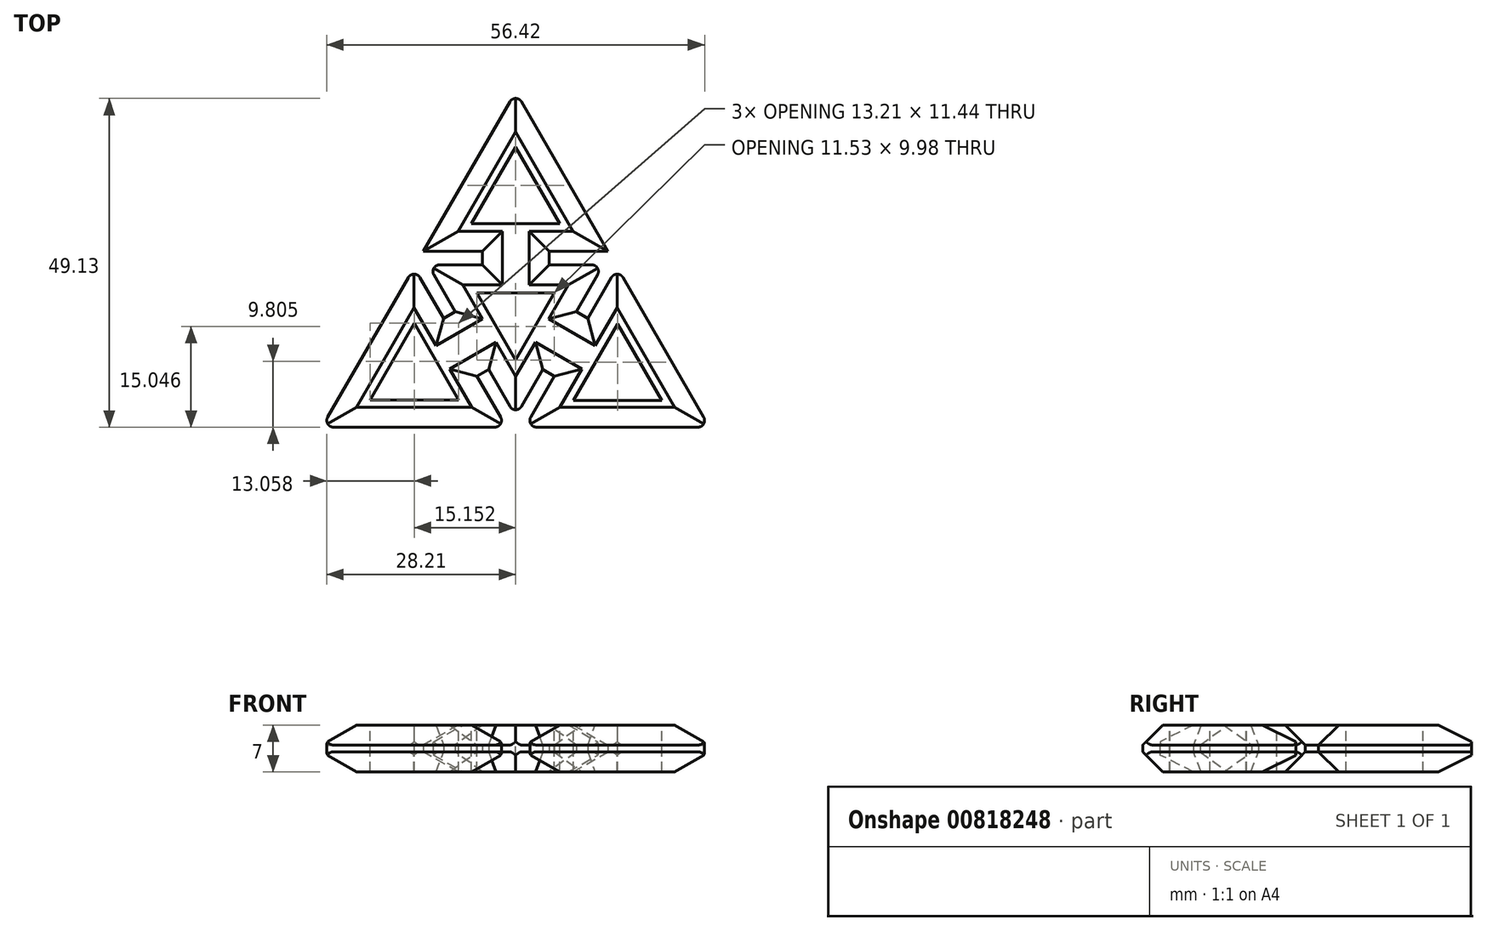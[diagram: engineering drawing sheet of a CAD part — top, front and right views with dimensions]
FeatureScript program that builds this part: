
annotation { "Feature Type Name" : "Feature", "Feature Type Description" : "" }
export const myFeature = defineFeature(function(context is Context, id is Id, definition is map)
    precondition{}
    {
        {
            var Q0;
            Q0=qCreatedBy(makeId("Top.planeOp"),FACE);
            var sketch = newSketch(context, id + "F0", { "sketchPlane" : qUnion([Q0])});
            skLineSegment(sketch, "E0.0", {"start": v(33.1, -19.1) * mm, "end": v(-33.1, -19.1) * mm});
            skLineSegment(sketch, "E0.1", {"start": v(-33.1, -19.1) * mm, "end": v(0, 38.22) * mm});
            skLineSegment(sketch, "E0.2", {"start": v(0, 38.22) * mm, "end": v(33.1, -19.1) * mm});
            skPoint(sketch, "E0.0.midPoint", {"position": v(0, -19.1) * mm});
            skLineSegment(sketch, "E1", {"start": v(0, 38.22) * mm, "end": v(0, -19.1) * mm});
            skLineSegment(sketch, "E2", {"start": v(0, -19.1) * mm, "end": v(-16.55, 9.55) * mm});
            skLineSegment(sketch, "E3", {"start": v(0, -19.1) * mm, "end": v(16.55, 9.55) * mm});
            skLineSegment(sketch, "E4", {"start": v(-16.55, 9.55) * mm, "end": v(16.55, 9.55) * mm});
            skPoint(sketch, "E0.cCircle.center.orphan", {"position": v(0, 0) * mm});
            skLineSegment(sketch, "E5.0", {"start": v(-13.08, 7.55) * mm, "end": v(13.08, 7.55) * mm});
            skLineSegment(sketch, "E5.1", {"start": v(0, -15.1) * mm, "end": v(-13.08, 7.55) * mm});
            skLineSegment(sketch, "E5.2", {"start": v(0, -15.1) * mm, "end": v(13.08, 7.55) * mm});
            skLineSegment(sketch, "E6", {"start": v(-8.27, -4.78) * mm, "end": v(-6.54, -3.78) * mm});
            skLineSegment(sketch, "E7", {"start": v(8.27, -4.78) * mm, "end": v(6.54, -3.78) * mm});
            skLineSegment(sketch, "E8", {"start": v(0, 9.55) * mm, "end": v(0, 7.55) * mm});
            skLineSegment(sketch, "E9.0", {"start": v(-6.38, -9.46) * mm, "end": v(-4.04, -8.1) * mm});
            skLineSegment(sketch, "E10.0", {"start": v(-11.38, -0.8) * mm, "end": v(-9.04, 0.55) * mm});
            skLineSegment(sketch, "E11.0", {"start": v(11.38, -0.8) * mm, "end": v(9.04, 0.55) * mm});
            skLineSegment(sketch, "E12.0", {"start": v(6.38, -9.46) * mm, "end": v(4.04, -8.1) * mm});
            skLineSegment(sketch, "E13.0", {"start": v(-5, 10.25) * mm, "end": v(-5, 7.55) * mm});
            skLineSegment(sketch, "E14.0", {"start": v(5, 10.25) * mm, "end": v(5, 7.55) * mm});
            skLineSegment(sketch, "E15.0", {"start": v(-28.94, -16.7) * mm, "end": v(0, 33.42) * mm});
            skLineSegment(sketch, "E15.1", {"start": v(28.94, -16.7) * mm, "end": v(-28.94, -16.7) * mm});
            skLineSegment(sketch, "E15.2", {"start": v(0, 33.42) * mm, "end": v(28.94, -16.7) * mm});
            skSolve(sketch);
        }
        {
            var Q0;
            {var subQ0=sQuery(id+"F0.wireOp",EDGE,"E5.1");var subQ2=sQuery(id+"F0.wireOp",EDGE,"E5.0");var subQ3=makeQuery(id+"F0.imprint","INTERSECT",VERTEX,{"derivedFrom":[subQ2,subQ0]});Q0=makeQuery(id+"F0.imprint","IMPRINT",FACE,{"disambiguationData":[TD([[makeQuery(id+"F0.imprint","IMPRINT",EDGE,{"disambiguationData":[TD([[subQ3,-1.0]])],"derivedFrom":subQ2}),-1.0]])]});}
            var Q1;
            {var subQ4=sQuery(id+"F0.wireOp",EDGE,"E5.0");var subQ5=makeQuery(id+"F0.imprint","INTERSECT",VERTEX,{"derivedFrom":[subQ4,sQuery(id+"F0.wireOp",EDGE,"E14.0")]});Q1=makeQuery(id+"F0.imprint","IMPRINT",FACE,{"disambiguationData":[TD([[makeQuery(id+"F0.imprint","IMPRINT",EDGE,{"disambiguationData":[TD([[subQ5,-1.0]])],"derivedFrom":subQ4}),-1.0]])]});}
            var Q2;
            {var subQ3=sQuery(id+"F0.wireOp",EDGE,"E6");Q2=makeQuery(id+"F0.imprint","IMPRINT",FACE,{"disambiguationData":[TD([[makeQuery(id+"F0.imprint","IMPRINT",EDGE,{"derivedFrom":subQ3}),1.0]])]});}
            var Q3;
            {var subQ0=sQuery(id+"F0.wireOp",EDGE,"E6");Q3=makeQuery(id+"F0.imprint","IMPRINT",FACE,{"disambiguationData":[TD([[makeQuery(id+"F0.imprint","IMPRINT",EDGE,{"derivedFrom":subQ0}),-1.0]])]});}
            var Q4;
            {var subQ0=sQuery(id+"F0.wireOp",EDGE,"E7");Q4=makeQuery(id+"F0.imprint","IMPRINT",FACE,{"disambiguationData":[TD([[makeQuery(id+"F0.imprint","IMPRINT",EDGE,{"derivedFrom":subQ0}),-1.0]])]});}
            var Q5;
            {var subQ0=sQuery(id+"F0.wireOp",EDGE,"E7");Q5=makeQuery(id+"F0.imprint","IMPRINT",FACE,{"disambiguationData":[TD([[makeQuery(id+"F0.imprint","IMPRINT",EDGE,{"derivedFrom":subQ0}),1.0]])]});}
            var Q6;
            {var subQ0=sQuery(id+"F0.wireOp",EDGE,"E4");var subQ1=sQuery(id+"F0.wireOp",EDGE,"E1");var subQ2=makeQuery(id+"F0.imprint","INTERSECT",VERTEX,{"derivedFrom":[subQ1,subQ0]});Q6=makeQuery(id+"F0.imprint","IMPRINT",FACE,{"disambiguationData":[TD([[makeQuery(id+"F0.imprint","IMPRINT",EDGE,{"disambiguationData":[TD([[subQ2,-1.0]])],"derivedFrom":subQ1}),1.0]])]});}
            var Q7;
            {var subQ0=sQuery(id+"F0.wireOp",EDGE,"E4");var subQ1=sQuery(id+"F0.wireOp",EDGE,"E1");var subQ2=makeQuery(id+"F0.imprint","INTERSECT",VERTEX,{"derivedFrom":[subQ1,subQ0]});Q7=makeQuery(id+"F0.imprint","IMPRINT",FACE,{"disambiguationData":[TD([[makeQuery(id+"F0.imprint","IMPRINT",EDGE,{"disambiguationData":[TD([[subQ2,-1.0]])],"derivedFrom":subQ1}),-1.0]])]});}
            var Q8;
            {var subQ0=sQuery(id+"F0.wireOp",EDGE,"E2");var subQ3=makeQuery(id+"F0.imprint","INTERSECT",VERTEX,{"derivedFrom":[subQ0,sQuery(id+"F0.wireOp",EDGE,"E10.0")]});Q8=makeQuery(id+"F0.imprint","IMPRINT",FACE,{"disambiguationData":[TD([[makeQuery(id+"F0.imprint","IMPRINT",EDGE,{"disambiguationData":[TD([[subQ3,-1.0]])],"derivedFrom":subQ0}),1.0]])]});}
            var Q9;
            {var subQ0=sQuery(id+"F0.wireOp",EDGE,"E3");var subQ4=sQuery(id+"F0.wireOp",EDGE,"E15.1");var subQ5=makeQuery(id+"F0.imprint","INTERSECT",VERTEX,{"derivedFrom":[subQ0,subQ4]});Q9=makeQuery(id+"F0.imprint","IMPRINT",FACE,{"disambiguationData":[TD([[makeQuery(id+"F0.imprint","IMPRINT",EDGE,{"disambiguationData":[TD([[subQ5,-1.0]])],"derivedFrom":subQ0}),-1.0]])]});}
            var Q10;
            {var subQ3=sQuery(id+"F0.wireOp",EDGE,"E4");var subQ5=makeQuery(id+"F0.imprint","INTERSECT",VERTEX,{"derivedFrom":[subQ3,sQuery(id+"F0.wireOp",EDGE,"E14.0")]});Q10=makeQuery(id+"F0.imprint","IMPRINT",FACE,{"disambiguationData":[TD([[makeQuery(id+"F0.imprint","IMPRINT",EDGE,{"disambiguationData":[TD([[subQ5,-1.0]])],"derivedFrom":subQ3}),1.0]])]});}
            var Q11;
            {var subQ0=sQuery(id+"F0.wireOp",EDGE,"E15.0");var subQ3=sQuery(id+"F0.wireOp",EDGE,"E4");var subQ6=makeQuery(id+"F0.imprint","INTERSECT",VERTEX,{"derivedFrom":[subQ3,subQ0]});Q11=makeQuery(id+"F0.imprint","IMPRINT",FACE,{"disambiguationData":[TD([[makeQuery(id+"F0.imprint","IMPRINT",EDGE,{"disambiguationData":[TD([[subQ6,-1.0]])],"derivedFrom":subQ3}),1.0]])]});}
            extrude(context, id + "F1", {"entities" : qUnion([Q0, Q1, Q2, Q3, Q4, Q5, Q6, Q7, Q8, Q9, Q10, Q11]), "depth" : 3.5 * mm, "offsetDistance" : 25 * mm});
        }
        {
            var Q0;
            Q0=makeQuery(id+"F1.opExtrude","CAP_FACE",FACE,{"disambiguationData":[OSD([sQuery(id+"F0.wireOp",EDGE,"E2"),sQuery(id+"F0.wireOp",EDGE,"E3"),sQuery(id+"F0.wireOp",EDGE,"E4"),sQuery(id+"F0.wireOp",EDGE,"E5.0"),sQuery(id+"F0.wireOp",EDGE,"E5.1"),sQuery(id+"F0.wireOp",EDGE,"E5.2"),sQuery(id+"F0.wireOp",EDGE,"E9.0"),sQuery(id+"F0.wireOp",EDGE,"E10.0"),sQuery(id+"F0.wireOp",EDGE,"E11.0"),sQuery(id+"F0.wireOp",EDGE,"E12.0"),sQuery(id+"F0.wireOp",EDGE,"E13.0"),sQuery(id+"F0.wireOp",EDGE,"E14.0"),sQuery(id+"F0.wireOp",EDGE,"E15.0"),sQuery(id+"F0.wireOp",EDGE,"E15.1"),sQuery(id+"F0.wireOp",EDGE,"E15.2")])],"isStart":false});
            chamfer(context, id + "F2", {"entities" : qUnion([Q0]), "width" : 3 * mm, "tangentPropagation" : true});
        }
        {
            var Q0;
            Q0=makeQuery(id+"F1.opExtrude","SWEPT_EDGE",EDGE,{"disambiguationData":[OSD([sQuery(id+"F0.wireOp",EDGE,"E15.0"),sQuery(id+"F0.wireOp",EDGE,"E15.1")])]});
            var Q1;
            Q1=makeQuery(id+"F1.opExtrude","SWEPT_EDGE",EDGE,{"disambiguationData":[OSD([sQuery(id+"F0.wireOp",EDGE,"E15.1"),sQuery(id+"F0.wireOp",EDGE,"E15.2")])]});
            var Q2;
            Q2=makeQuery(id+"F1.opExtrude","SWEPT_EDGE",EDGE,{"disambiguationData":[OSD([sQuery(id+"F0.wireOp",EDGE,"E1"),sQuery(id+"F0.wireOp",EDGE,"E15.0"),sQuery(id+"F0.wireOp",EDGE,"E15.2")])]});
            var Q3;
            Q3=makeQuery(id+"F1.opExtrude","SWEPT_EDGE",EDGE,{"disambiguationData":[OSD([sQuery(id+"F0.wireOp",EDGE,"E2"),sQuery(id+"F0.wireOp",EDGE,"E15.0")])]});
            var Q4;
            Q4=makeQuery(id+"F1.opExtrude","SWEPT_EDGE",EDGE,{"disambiguationData":[OSD([sQuery(id+"F0.wireOp",EDGE,"E3"),sQuery(id+"F0.wireOp",EDGE,"E15.2")])]});
            var Q5;
            Q5=makeQuery(id+"F1.opExtrude","SWEPT_EDGE",EDGE,{"disambiguationData":[OSD([sQuery(id+"F0.wireOp",EDGE,"E2"),sQuery(id+"F0.wireOp",EDGE,"E15.1")])]});
            var Q6;
            Q6=makeQuery(id+"F1.opExtrude","SWEPT_EDGE",EDGE,{"disambiguationData":[OSD([sQuery(id+"F0.wireOp",EDGE,"E3"),sQuery(id+"F0.wireOp",EDGE,"E15.1")])]});
            var Q7;
            Q7=makeQuery(id+"F1.opExtrude","SWEPT_EDGE",EDGE,{"disambiguationData":[OSD([sQuery(id+"F0.wireOp",EDGE,"E5.0"),sQuery(id+"F0.wireOp",EDGE,"E5.1")])]});
            var Q8;
            Q8=makeQuery(id+"F1.opExtrude","SWEPT_EDGE",EDGE,{"disambiguationData":[OSD([sQuery(id+"F0.wireOp",EDGE,"E5.0"),sQuery(id+"F0.wireOp",EDGE,"E5.2")])]});
            var Q9;
            Q9=makeQuery(id+"F1.opExtrude","SWEPT_EDGE",EDGE,{"disambiguationData":[OSD([sQuery(id+"F0.wireOp",EDGE,"E1"),sQuery(id+"F0.wireOp",EDGE,"E5.1"),sQuery(id+"F0.wireOp",EDGE,"E5.2")])]});
            fillet(context, id + "F3", {"entities" : qUnion([Q0, Q1, Q2, Q3, Q4, Q5, Q6, Q7, Q8, Q9]), "radius" : 1 * mm, "tangentPropagation" : true, "allowEdgeOverflow" : false});
        }
        {
            var Q0;
            Q0=makeQuery(id+"F1.opExtrude","SWEPT_BODY",BODY,{"disambiguationData":[OSD([sQuery(id+"F0.wireOp",EDGE,"E2"),sQuery(id+"F0.wireOp",EDGE,"E3"),sQuery(id+"F0.wireOp",EDGE,"E4"),sQuery(id+"F0.wireOp",EDGE,"E5.0"),sQuery(id+"F0.wireOp",EDGE,"E5.1"),sQuery(id+"F0.wireOp",EDGE,"E5.2"),sQuery(id+"F0.wireOp",EDGE,"E9.0"),sQuery(id+"F0.wireOp",EDGE,"E10.0"),sQuery(id+"F0.wireOp",EDGE,"E11.0"),sQuery(id+"F0.wireOp",EDGE,"E12.0"),sQuery(id+"F0.wireOp",EDGE,"E13.0"),sQuery(id+"F0.wireOp",EDGE,"E14.0"),sQuery(id+"F0.wireOp",EDGE,"E15.0"),sQuery(id+"F0.wireOp",EDGE,"E15.1"),sQuery(id+"F0.wireOp",EDGE,"E15.2")])]});
            var Q1;
            Q1=qCreatedBy(makeId("Top.planeOp"),FACE);
            mirror(context, id + "F4", {"operationType" : NewBodyOperationType.ADD, "entities" : qUnion([Q0]), "mirrorPlane" : qUnion([Q1])});
        }
        {
            var Q0;
            Q0=makeQuery(id+"F1.opExtrude","CAP_FACE",FACE,{"disambiguationData":[OSD([sQuery(id+"F0.wireOp",EDGE,"E2"),sQuery(id+"F0.wireOp",EDGE,"E3"),sQuery(id+"F0.wireOp",EDGE,"E4"),sQuery(id+"F0.wireOp",EDGE,"E5.0"),sQuery(id+"F0.wireOp",EDGE,"E5.1"),sQuery(id+"F0.wireOp",EDGE,"E5.2"),sQuery(id+"F0.wireOp",EDGE,"E9.0"),sQuery(id+"F0.wireOp",EDGE,"E10.0"),sQuery(id+"F0.wireOp",EDGE,"E11.0"),sQuery(id+"F0.wireOp",EDGE,"E12.0"),sQuery(id+"F0.wireOp",EDGE,"E13.0"),sQuery(id+"F0.wireOp",EDGE,"E14.0"),sQuery(id+"F0.wireOp",EDGE,"E15.0"),sQuery(id+"F0.wireOp",EDGE,"E15.1"),sQuery(id+"F0.wireOp",EDGE,"E15.2")])],"isStart":false});
            var sketch = newSketch(context, id + "F5", { "sketchPlane" : qUnion([Q0])});
            skCircle(sketch, "E16.cCircle", {"center": v(0, 17.5) * mm, "radius": 3.81 * mm, "construction": true});
            skLineSegment(sketch, "E16.0", {"start": v(6.6, 13.69) * mm, "end": v(-6.6, 13.69) * mm});
            skLineSegment(sketch, "E16.1", {"start": v(-6.6, 13.69) * mm, "end": v(0, 25.13) * mm});
            skLineSegment(sketch, "E16.2", {"start": v(0, 25.13) * mm, "end": v(6.6, 13.69) * mm});
            skPoint(sketch, "E16.0.midPoint", {"position": v(0, 13.69) * mm});
            skCircle(sketch, "E17.cCircle", {"center": v(-15.15, -8.81) * mm, "radius": 3.81 * mm, "construction": true});
            skLineSegment(sketch, "E17.0", {"start": v(-8.55, -12.63) * mm, "end": v(-21.76, -12.63) * mm});
            skLineSegment(sketch, "E17.1", {"start": v(-21.76, -12.63) * mm, "end": v(-15.15, -1.19) * mm});
            skLineSegment(sketch, "E17.2", {"start": v(-15.15, -1.19) * mm, "end": v(-8.55, -12.63) * mm});
            skPoint(sketch, "E17.0.midPoint", {"position": v(-15.15, -12.63) * mm});
            skCircle(sketch, "E18.cCircle", {"center": v(15.23, -8.9) * mm, "radius": 3.81 * mm, "construction": true});
            skLineSegment(sketch, "E18.0", {"start": v(21.84, -12.72) * mm, "end": v(8.63, -12.72) * mm});
            skLineSegment(sketch, "E18.1", {"start": v(8.63, -12.72) * mm, "end": v(15.23, -1.28) * mm});
            skLineSegment(sketch, "E18.2", {"start": v(15.23, -1.28) * mm, "end": v(21.84, -12.72) * mm});
            skPoint(sketch, "E18.0.midPoint", {"position": v(15.23, -12.72) * mm});
            skCircle(sketch, "E19.cCircle", {"center": v(0, 0) * mm, "radius": 3.33 * mm, "construction": true});
            skLineSegment(sketch, "E19.0", {"start": v(0, -6.65) * mm, "end": v(-5.76, 3.33) * mm});
            skLineSegment(sketch, "E19.1", {"start": v(-5.76, 3.33) * mm, "end": v(5.76, 3.33) * mm});
            skLineSegment(sketch, "E19.2", {"start": v(5.76, 3.33) * mm, "end": v(0, -6.65) * mm});
            skPoint(sketch, "E19.0.midPoint", {"position": v(-2.88, -1.66) * mm});
            skSolve(sketch);
        }
        {
            var Q0;
            Q0=qSketchRegion(id+"F5",true);
            extrude(context, id + "F6", {"entities" : qUnion([Q0]), "operationType" : NewBodyOperationType.REMOVE, "oppositeDirection" : true, "depth" : 9.2 * mm, "offsetDistance" : 25 * mm});
        }
    });
